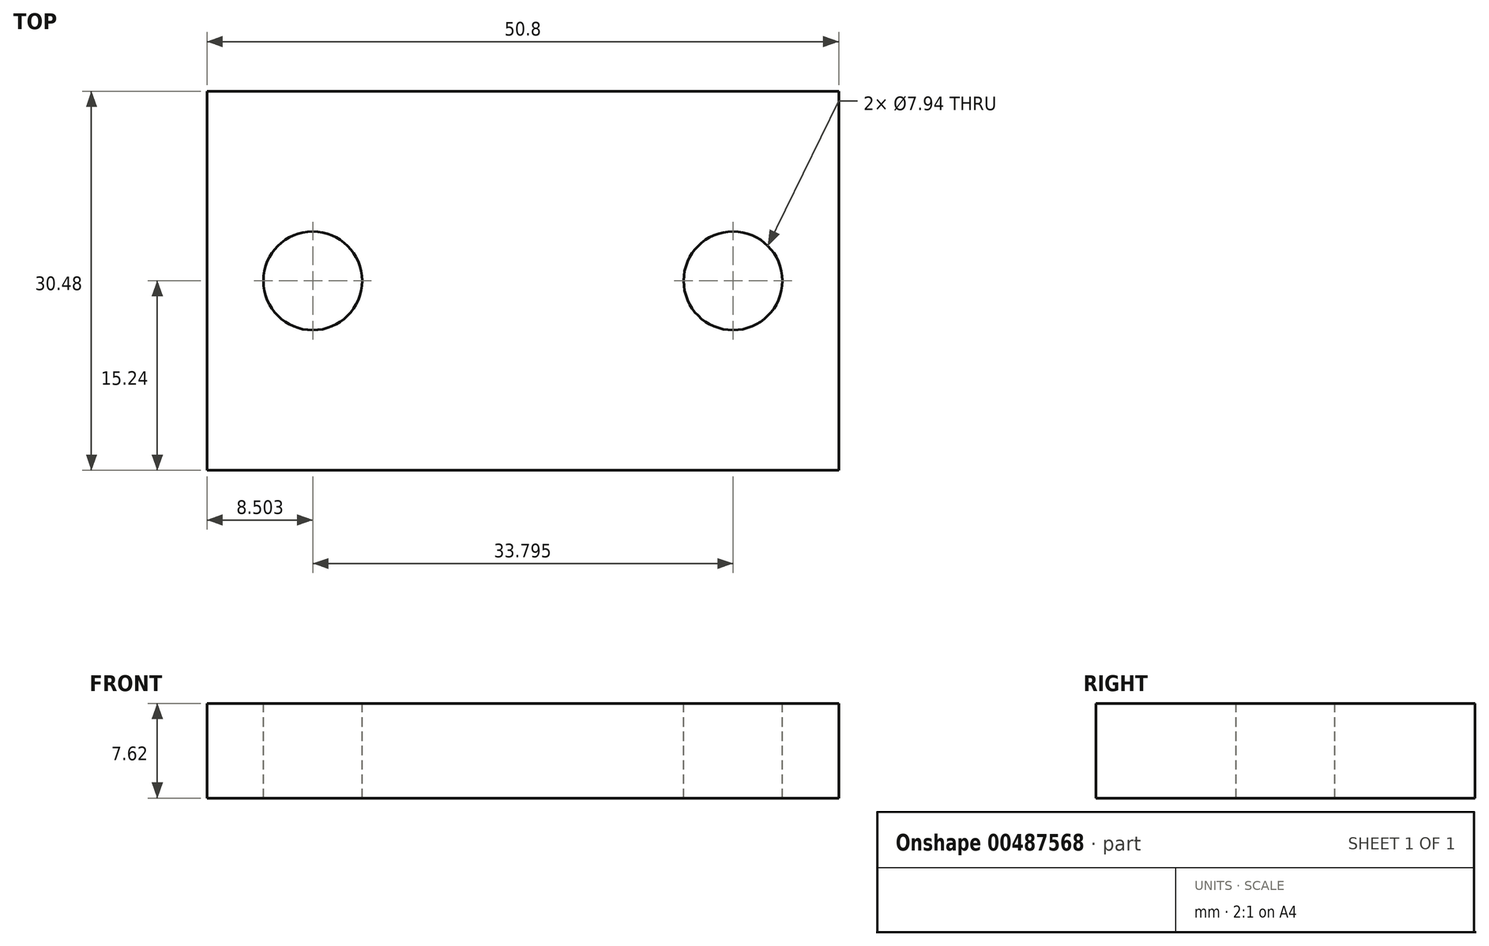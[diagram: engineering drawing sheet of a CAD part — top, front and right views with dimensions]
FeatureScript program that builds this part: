
annotation { "Feature Type Name" : "Feature", "Feature Type Description" : "" }
export const myFeature = defineFeature(function(context is Context, id is Id, definition is map)
    precondition{}
    {
        {
            var Q0;
            Q0=qCreatedBy(makeId("Top.planeOp"),FACE);
            var sketch = newSketch(context, id + "F0", { "sketchPlane" : qUnion([Q0])});
            skLineSegment(sketch, "E0.bottom", {"start": v(25.4, 15.24) * mm, "end": v(-25.4, 15.24) * mm});
            skLineSegment(sketch, "E0.top", {"start": v(25.4, -15.24) * mm, "end": v(-25.4, -15.24) * mm});
            skLineSegment(sketch, "E0.left", {"start": v(25.4, 15.24) * mm, "end": v(25.4, -15.24) * mm});
            skLineSegment(sketch, "E0.right", {"start": v(-25.4, 15.24) * mm, "end": v(-25.4, -15.24) * mm});
            skPoint(sketch, "E0.middle", {"position": v(0, 0) * mm});
            skSolve(sketch);
        }
        {
            var Q0;
            Q0 = qSketchRegion(id + "F0", true);
            extrude(context, id + "F1", {"entities" : qUnion([Q0]), "depth" : 7.62 * mm});
        }
        {
            var Q0;
            Q0=makeQuery(id+"F1.opExtrude","CAP_FACE",FACE,{"disambiguationData":[OSD([sQuery(id+"F0.wireOp",EDGE,"E0.bottom"),sQuery(id+"F0.wireOp",EDGE,"E0.top"),sQuery(id+"F0.wireOp",EDGE,"E0.left"),sQuery(id+"F0.wireOp",EDGE,"E0.right")])],"isStart":false});
            var sketch = newSketch(context, id + "F2", { "sketchPlane" : qUnion([Q0])});
            skLineSegment(sketch, "E1", {"start": v(-25.4, 0) * mm, "end": v(25.4, 0) * mm, "construction": true});
            skCircle(sketch, "E2", {"center": v(-16.9, 0) * mm, "radius": 3.97 * mm});
            skCircle(sketch, "E3", {"center": v(16.9, 0) * mm, "radius": 3.97 * mm});
            skLineSegment(sketch, "E4", {"start": v(-25.4, 0) * mm, "end": v(-20.87, 0) * mm});
            skLineSegment(sketch, "E5", {"start": v(25.4, 0) * mm, "end": v(20.87, 0) * mm});
            skSolve(sketch);
        }
        {
            var Q0;
            Q0 = qSketchRegion(id + "F2", true);
            extrude(context, id + "F3", {"entities" : qUnion([Q0]), "operationType" : NewBodyOperationType.REMOVE, "oppositeDirection" : true, "depth" : 25.4 * mm});
        }
    });
